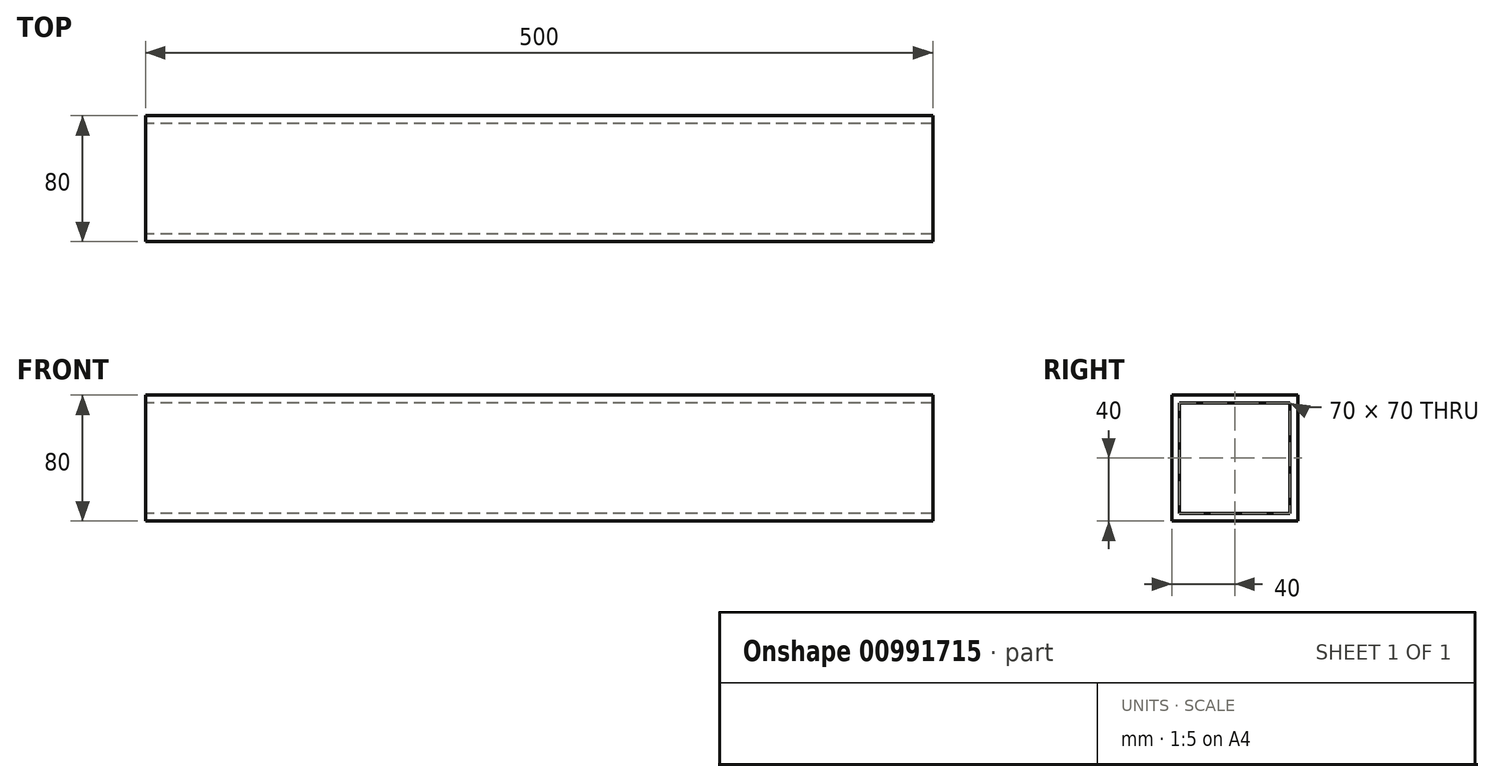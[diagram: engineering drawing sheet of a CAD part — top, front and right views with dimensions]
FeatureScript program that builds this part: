
annotation { "Feature Type Name" : "Feature", "Feature Type Description" : "" }
export const myFeature = defineFeature(function(context is Context, id is Id, definition is map)
    precondition{}
    {
        {
            var Q0;
            Q0=qCreatedBy(makeId("Right.planeOp"),FACE);
            var sketch = newSketch(context, id + "F0", { "sketchPlane" : qUnion([Q0])});
            skLineSegment(sketch, "E0.bottom", {"start": v(-40, 40) * mm, "end": v(40, 40) * mm});
            skLineSegment(sketch, "E0.top", {"start": v(-40, -40) * mm, "end": v(40, -40) * mm});
            skLineSegment(sketch, "E0.left", {"start": v(-40, 40) * mm, "end": v(-40, -40) * mm});
            skLineSegment(sketch, "E0.right", {"start": v(40, 40) * mm, "end": v(40, -40) * mm});
            skLineSegment(sketch, "E1.0", {"start": v(-35, 35) * mm, "end": v(35, 35) * mm});
            skLineSegment(sketch, "E1.1", {"start": v(-35, 35) * mm, "end": v(-35, -35) * mm});
            skLineSegment(sketch, "E1.2", {"start": v(-35, -35) * mm, "end": v(35, -35) * mm});
            skLineSegment(sketch, "E1.3", {"start": v(35, 35) * mm, "end": v(35, -35) * mm});
            skSolve(sketch);
        }
        {
            var Q0;
            Q0=makeQuery(id+"F0.imprint","IMPRINT",FACE,{"disambiguationData":[TD([[makeQuery(id+"F0.imprint","IMPRINT",EDGE,{"derivedFrom":sQuery(id+"F0.wireOp",EDGE,"E0.bottom")}),-1.0]])]});
            extrude(context, id + "F1", {"entities" : qUnion([Q0]), "depth" : 500 * mm, "offsetDistance" : 25 * mm});
        }
    });
